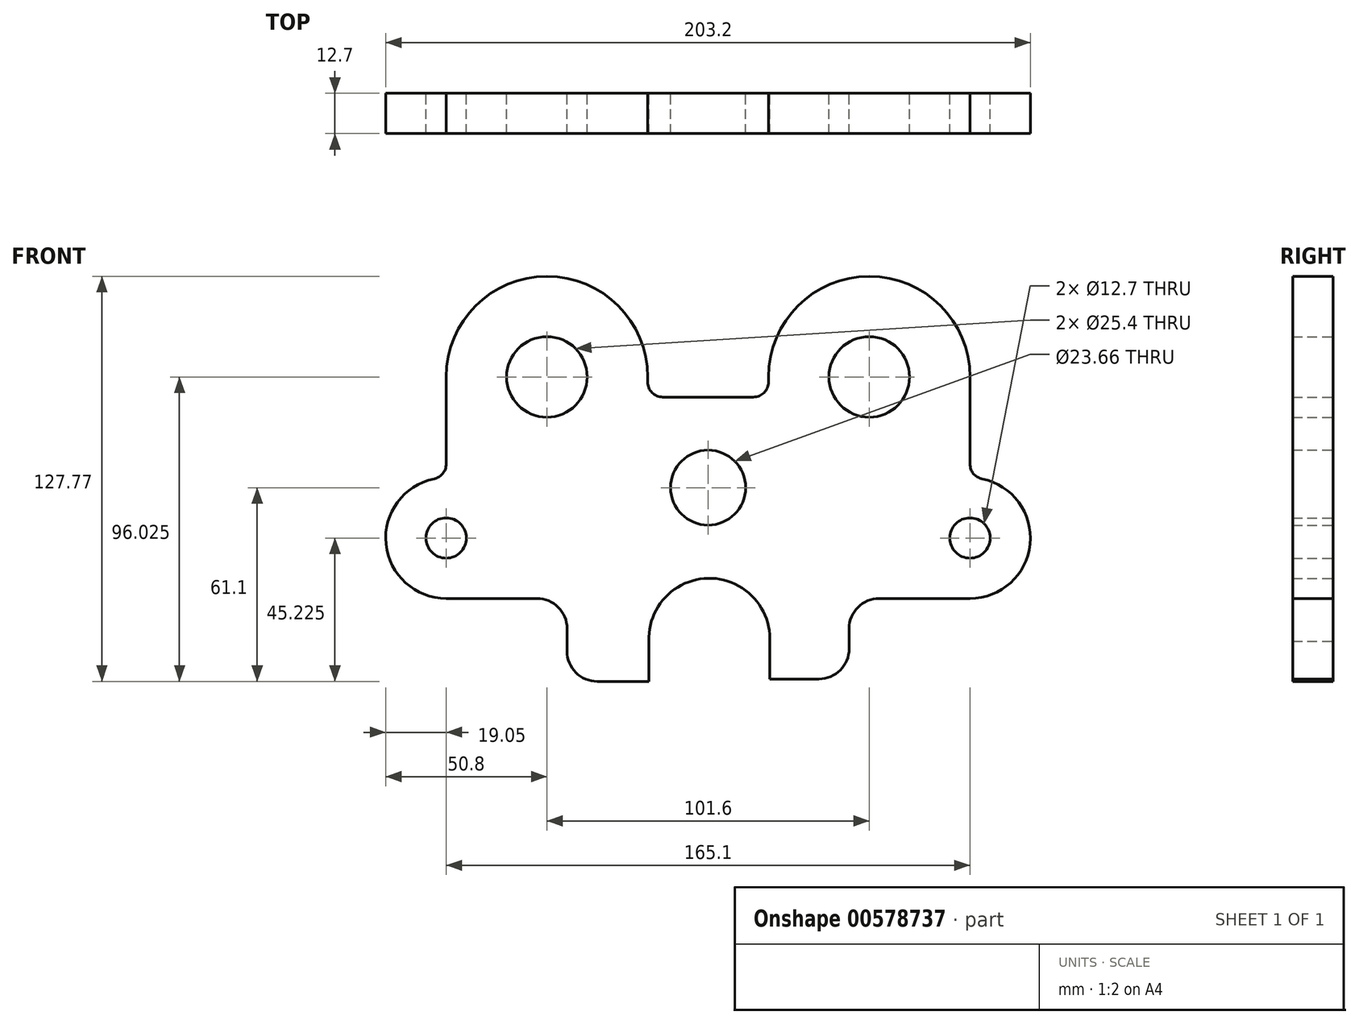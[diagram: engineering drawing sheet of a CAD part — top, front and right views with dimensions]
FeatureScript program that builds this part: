
annotation { "Feature Type Name" : "Feature", "Feature Type Description" : "" }
export const myFeature = defineFeature(function(context is Context, id is Id, definition is map)
    precondition{}
    {
        {
            var Q0;
            Q0=qCreatedBy(makeId("Front.planeOp"),FACE);
            var sketch = newSketch(context, id + "F0", { "sketchPlane" : qUnion([Q0])});
            skArc(sketch, "E0", {"start": v(82.55, 34.93) * mm, "mid": v(50.8, 66.68) * mm, "end": v(19.05, 34.93) * mm});
            skArc(sketch, "E1", {"start": v(-19.05, 34.93) * mm, "mid": v(-50.8, 66.68) * mm, "end": v(-82.55, 34.93) * mm});
            skLineSegment(sketch, "E2", {"start": v(-82.55, 34.92) * mm, "end": v(-82.55, 7.46) * mm});
            skLineSegment(sketch, "E3", {"start": v(82.55, 34.93) * mm, "end": v(82.55, 7.46) * mm});
            skCircle(sketch, "E4", {"center": v(50.8, 34.93) * mm, "radius": 12.7 * mm});
            skCircle(sketch, "E5", {"center": v(-50.8, 34.93) * mm, "radius": 12.7 * mm});
            skLineSegment(sketch, "E6", {"start": v(0, 94.12) * mm, "end": v(0, -101.3) * mm, "construction": true});
            skArc(sketch, "E7", {"start": v(-86.36, 2.8) * mm, "mid": v(-101.5, -17.79) * mm, "end": v(-82.55, -34.92) * mm});
            skArc(sketch, "E8", {"start": v(82.55, -34.92) * mm, "mid": v(101.5, -17.79) * mm, "end": v(86.36, 2.8) * mm});
            skLineSegment(sketch, "E9", {"start": v(82.55, -34.92) * mm, "end": v(53.98, -34.92) * mm});
            skLineSegment(sketch, "E10", {"start": v(-82.55, -34.92) * mm, "end": v(-53.97, -34.92) * mm});
            skLineSegment(sketch, "E11", {"start": v(-44.45, -44.45) * mm, "end": v(-44.45, -51.58) * mm});
            skLineSegment(sketch, "E12", {"start": v(-34.92, -61.1) * mm, "end": v(-18.63, -61.1) * mm});
            skLineSegment(sketch, "E13", {"start": v(44.45, -44.45) * mm, "end": v(44.45, -50.8) * mm});
            skLineSegment(sketch, "E14", {"start": v(34.93, -60.32) * mm, "end": v(19.45, -60.32) * mm});
            skLineSegment(sketch, "E15", {"start": v(-18.63, -61.1) * mm, "end": v(-18.63, -48.4) * mm});
            skLineSegment(sketch, "E16", {"start": v(19.45, -60.33) * mm, "end": v(19.45, -47.62) * mm});
            skArc(sketch, "E17", {"start": v(19.45, -47.62) * mm, "mid": v(0.01, -28.58) * mm, "end": v(-18.63, -48.4) * mm});
            skCircle(sketch, "E18", {"center": v(-82.55, -15.88) * mm, "radius": 6.35 * mm});
            skCircle(sketch, "E19", {"center": v(82.55, -15.87) * mm, "radius": 6.35 * mm});
            skCircle(sketch, "E20", {"center": v(0, 0) * mm, "radius": 11.83 * mm});
            skLineSegment(sketch, "E21", {"start": v(-19.05, 34.92) * mm, "end": v(-19.05, 33.34) * mm});
            skLineSegment(sketch, "E22", {"start": v(19.05, 34.93) * mm, "end": v(19.05, 33.34) * mm});
            skLineSegment(sketch, "E23", {"start": v(-14.29, 28.58) * mm, "end": v(14.29, 28.58) * mm});
            skPoint(sketch, "E24.visualSharp", {"position": v(-19.05, 28.58) * mm});
            skArc(sketch, "E24.filletArc", {"start": v(-19.05, 33.34) * mm, "mid": v(-17.66, 29.97) * mm, "end": v(-14.29, 28.58) * mm});
            skPoint(sketch, "E25.visualSharp", {"position": v(19.05, 28.58) * mm});
            skArc(sketch, "E25.filletArc", {"start": v(14.29, 28.58) * mm, "mid": v(17.66, 29.97) * mm, "end": v(19.05, 33.34) * mm});
            skPoint(sketch, "E26.visualSharp", {"position": v(44.45, -34.92) * mm});
            skArc(sketch, "E26.filletArc", {"start": v(53.98, -34.92) * mm, "mid": v(47.24, -37.71) * mm, "end": v(44.45, -44.45) * mm});
            skPoint(sketch, "E27.visualSharp", {"position": v(44.45, -60.32) * mm});
            skArc(sketch, "E27.filletArc", {"start": v(34.93, -60.32) * mm, "mid": v(41.66, -57.54) * mm, "end": v(44.45, -50.8) * mm});
            skPoint(sketch, "E28.visualSharp", {"position": v(-44.45, -61.1) * mm});
            skArc(sketch, "E28.filletArc", {"start": v(-44.45, -51.58) * mm, "mid": v(-41.66, -58.31) * mm, "end": v(-34.92, -61.1) * mm});
            skPoint(sketch, "E29.visualSharp", {"position": v(-44.45, -34.92) * mm});
            skArc(sketch, "E29.filletArc", {"start": v(-44.45, -44.45) * mm, "mid": v(-47.24, -37.71) * mm, "end": v(-53.97, -34.93) * mm});
            skPoint(sketch, "E30.visualSharp", {"position": v(-82.55, 3.18) * mm});
            skArc(sketch, "E30.filletArc", {"start": v(-86.36, 2.8) * mm, "mid": v(-83.62, 4.44) * mm, "end": v(-82.55, 7.46) * mm});
            skPoint(sketch, "E31.visualSharp", {"position": v(82.55, 3.18) * mm});
            skArc(sketch, "E31.filletArc", {"start": v(82.55, 7.46) * mm, "mid": v(83.62, 4.44) * mm, "end": v(86.36, 2.8) * mm});
            skCircle(sketch, "E32", {"center": v(-82.55, -15.88) * mm, "radius": 7.94 * mm});
            skCircle(sketch, "E33", {"center": v(82.55, -15.87) * mm, "radius": 7.94 * mm});
            skSolve(sketch);
        }
        {
            var Q0;
            Q0=qSketchRegion(id+"F0",true);
            var Q1;
            Q1=makeQuery(id+"F0.imprint","IMPRINT",FACE,{"disambiguationData":[TD([[makeQuery(id+"F0.imprint","IMPRINT",EDGE,{"derivedFrom":sQuery(id+"F0.wireOp",EDGE,"E18")}),-1.0]])]});
            var Q2;
            Q2=makeQuery(id+"F0.imprint","IMPRINT",FACE,{"disambiguationData":[TD([[makeQuery(id+"F0.imprint","IMPRINT",EDGE,{"derivedFrom":sQuery(id+"F0.wireOp",EDGE,"E19")}),-1.0]])]});
            extrude(context, id + "F1", {"entities" : qUnion([Q0, Q1, Q2]), "depth" : 12.7 * mm, "offsetDistance" : 25.4 * mm});
        }
    });
